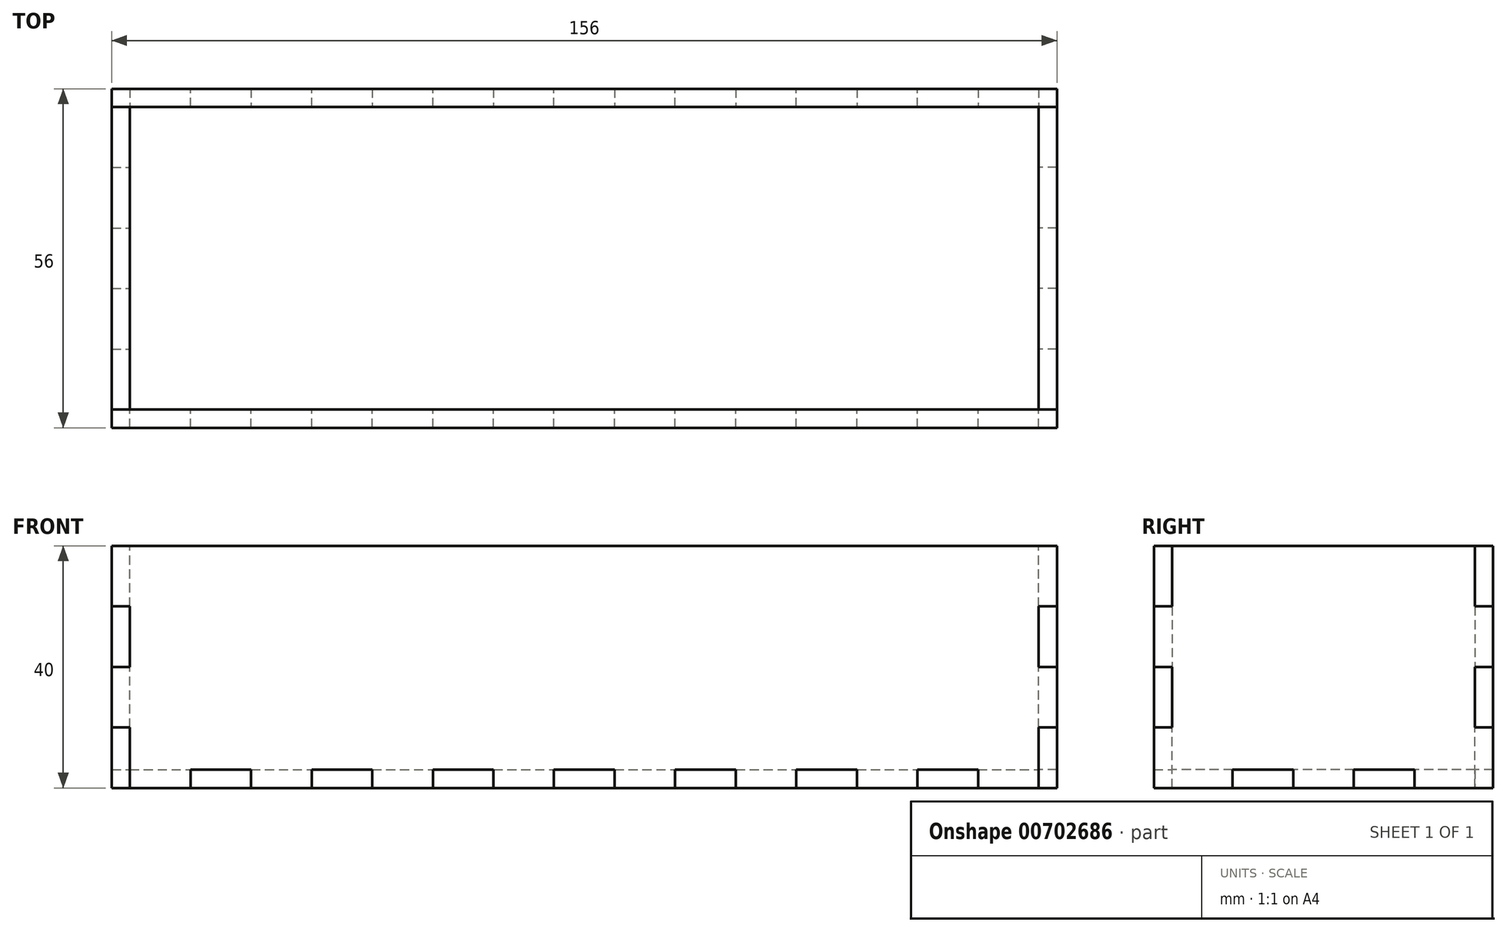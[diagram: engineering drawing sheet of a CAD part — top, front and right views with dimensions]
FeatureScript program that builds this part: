
annotation { "Feature Type Name" : "Feature", "Feature Type Description" : "" }
export const myFeature = defineFeature(function(context is Context, id is Id, definition is map)
    precondition{}
    {
        {
            var Q0;
            Q0=qCreatedBy(makeId("Top.planeOp"),FACE);
            var sketch = newSketch(context, id + "F0", { "sketchPlane" : qUnion([Q0])});
            skPoint(sketch, "E0.middle", {"position": v(0, 0) * mm});
            skLineSegment(sketch, "E1", {"start": v(-75, -25) * mm, "end": v(-65, -25) * mm});
            skLineSegment(sketch, "E2", {"start": v(-65, -25) * mm, "end": v(-65, -28) * mm});
            skLineSegment(sketch, "E3", {"start": v(-65, -28) * mm, "end": v(-55, -28) * mm});
            skLineSegment(sketch, "E4", {"start": v(-55, -28) * mm, "end": v(-55, -25) * mm});
            skLineSegment(sketch, "E5", {"start": v(-55, -25) * mm, "end": v(-45, -25) * mm});
            skLineSegment(sketch, "E6", {"start": v(-45, -25) * mm, "end": v(-45, -28) * mm});
            skLineSegment(sketch, "E7", {"start": v(-45, -28) * mm, "end": v(-35, -28) * mm});
            skLineSegment(sketch, "E8", {"start": v(-35, -28) * mm, "end": v(-35, -25) * mm});
            skLineSegment(sketch, "E9", {"start": v(-35, -25) * mm, "end": v(-25, -25) * mm});
            skLineSegment(sketch, "E10", {"start": v(-25, -25) * mm, "end": v(-25, -28) * mm});
            skLineSegment(sketch, "E11", {"start": v(-25, -28) * mm, "end": v(-15, -28) * mm});
            skLineSegment(sketch, "E12", {"start": v(-15, -28) * mm, "end": v(-15, -25) * mm});
            skLineSegment(sketch, "E13", {"start": v(-15, -25) * mm, "end": v(-5, -25) * mm});
            skLineSegment(sketch, "E14", {"start": v(-5, -25) * mm, "end": v(-5, -28) * mm});
            skLineSegment(sketch, "E15", {"start": v(-5, -28) * mm, "end": v(5, -28) * mm});
            skLineSegment(sketch, "E16", {"start": v(5, -28) * mm, "end": v(5, -25) * mm});
            skLineSegment(sketch, "E17", {"start": v(5, -25) * mm, "end": v(15, -25) * mm});
            skLineSegment(sketch, "E18", {"start": v(15, -25) * mm, "end": v(15, -28) * mm});
            skLineSegment(sketch, "E19", {"start": v(15, -28) * mm, "end": v(25, -28) * mm});
            skLineSegment(sketch, "E20", {"start": v(25, -28) * mm, "end": v(25, -25) * mm});
            skLineSegment(sketch, "E21", {"start": v(25, -25) * mm, "end": v(35, -25) * mm});
            skLineSegment(sketch, "E22", {"start": v(35, -25) * mm, "end": v(35, -28) * mm});
            skLineSegment(sketch, "E23", {"start": v(35, -28) * mm, "end": v(45, -28) * mm});
            skLineSegment(sketch, "E24", {"start": v(45, -28) * mm, "end": v(45, -25) * mm});
            skLineSegment(sketch, "E25", {"start": v(45, -25) * mm, "end": v(55, -25) * mm});
            skLineSegment(sketch, "E26", {"start": v(55, -25) * mm, "end": v(55, -28) * mm});
            skLineSegment(sketch, "E27", {"start": v(55, -28) * mm, "end": v(65, -28) * mm});
            skLineSegment(sketch, "E28", {"start": v(65, -28) * mm, "end": v(65, -25) * mm});
            skLineSegment(sketch, "E29", {"start": v(65, -25) * mm, "end": v(75, -25) * mm});
            skLineSegment(sketch, "E30", {"start": v(-18.9, 0) * mm, "end": v(19.68, 0) * mm, "construction": true});
            skLineSegment(sketch, "E31", {"start": v(0, -7.18) * mm, "end": v(0, 9.4) * mm, "construction": true});
            skLineSegment(sketch, "E32.MirrorCS", {"start": v(35, 25) * mm, "end": v(35, 28) * mm});
            skLineSegment(sketch, "E33.MirrorCS", {"start": v(15, 25) * mm, "end": v(15, 28) * mm});
            skLineSegment(sketch, "E34.MirrorCS", {"start": v(-45, 25) * mm, "end": v(-45, 28) * mm});
            skLineSegment(sketch, "E35.MirrorCS", {"start": v(65, 28) * mm, "end": v(65, 25) * mm});
            skLineSegment(sketch, "E36.MirrorCS", {"start": v(-65, 25) * mm, "end": v(-65, 28) * mm});
            skLineSegment(sketch, "E37.MirrorCS", {"start": v(25, 28) * mm, "end": v(25, 25) * mm});
            skLineSegment(sketch, "E38.MirrorCS", {"start": v(5, 28) * mm, "end": v(5, 25) * mm});
            skLineSegment(sketch, "E39.MirrorCS", {"start": v(-15, 28) * mm, "end": v(-15, 25) * mm});
            skLineSegment(sketch, "E40.MirrorCS", {"start": v(-25, 25) * mm, "end": v(-25, 28) * mm});
            skLineSegment(sketch, "E41.MirrorCS", {"start": v(-75, 25) * mm, "end": v(-65, 25) * mm});
            skLineSegment(sketch, "E42.MirrorCS", {"start": v(-55, 28) * mm, "end": v(-55, 25) * mm});
            skLineSegment(sketch, "E43.MirrorCS", {"start": v(-35, 28) * mm, "end": v(-35, 25) * mm});
            skLineSegment(sketch, "E44.MirrorCS", {"start": v(55, 25) * mm, "end": v(55, 28) * mm});
            skLineSegment(sketch, "E45.MirrorCS", {"start": v(-5, 25) * mm, "end": v(-5, 28) * mm});
            skLineSegment(sketch, "E46.MirrorCS", {"start": v(45, 28) * mm, "end": v(45, 25) * mm});
            skLineSegment(sketch, "E47.MirrorCS", {"start": v(-55, 25) * mm, "end": v(-45, 25) * mm});
            skLineSegment(sketch, "E48.MirrorCS", {"start": v(-15, 25) * mm, "end": v(-5, 25) * mm});
            skLineSegment(sketch, "E49.MirrorCS", {"start": v(5, 25) * mm, "end": v(15, 25) * mm});
            skLineSegment(sketch, "E50.MirrorCS", {"start": v(25, 25) * mm, "end": v(35, 25) * mm});
            skLineSegment(sketch, "E51.MirrorCS", {"start": v(-35, 25) * mm, "end": v(-25, 25) * mm});
            skLineSegment(sketch, "E52.MirrorCS", {"start": v(45, 25) * mm, "end": v(55, 25) * mm});
            skLineSegment(sketch, "E53.MirrorCS", {"start": v(-45, 28) * mm, "end": v(-35, 28) * mm});
            skLineSegment(sketch, "E54.MirrorCS", {"start": v(-25, 28) * mm, "end": v(-15, 28) * mm});
            skLineSegment(sketch, "E55.MirrorCS", {"start": v(-5, 28) * mm, "end": v(5, 28) * mm});
            skLineSegment(sketch, "E56.MirrorCS", {"start": v(55, 28) * mm, "end": v(65, 28) * mm});
            skLineSegment(sketch, "E57.MirrorCS", {"start": v(-65, 28) * mm, "end": v(-55, 28) * mm});
            skLineSegment(sketch, "E58.MirrorCS", {"start": v(65, 25) * mm, "end": v(75, 25) * mm});
            skLineSegment(sketch, "E59.MirrorCS", {"start": v(35, 28) * mm, "end": v(45, 28) * mm});
            skLineSegment(sketch, "E60.MirrorCS", {"start": v(15, 28) * mm, "end": v(25, 28) * mm});
            skPoint(sketch, "E0.right.end.orphan", {"position": v(-75, 25) * mm});
            skLineSegment(sketch, "E61", {"start": v(-75, 25) * mm, "end": v(-75, 15) * mm});
            skLineSegment(sketch, "E62", {"start": v(-75, 15) * mm, "end": v(-78, 15) * mm});
            skLineSegment(sketch, "E63", {"start": v(-78, 15) * mm, "end": v(-78, 5) * mm});
            skLineSegment(sketch, "E64", {"start": v(-78, 5) * mm, "end": v(-75, 5) * mm});
            skLineSegment(sketch, "E65", {"start": v(-75, 5) * mm, "end": v(-75, -5) * mm});
            skLineSegment(sketch, "E66", {"start": v(-75, -5) * mm, "end": v(-78, -5) * mm});
            skLineSegment(sketch, "E67", {"start": v(-78, -5) * mm, "end": v(-78, -15) * mm});
            skLineSegment(sketch, "E68", {"start": v(-78, -15) * mm, "end": v(-75, -15) * mm});
            skLineSegment(sketch, "E69", {"start": v(-75, -15) * mm, "end": v(-75, -25) * mm});
            skPoint(sketch, "E0.left.end.orphan", {"position": v(75, 25) * mm});
            skLineSegment(sketch, "E70.MirrorCS", {"start": v(75, 15) * mm, "end": v(78, 15) * mm});
            skLineSegment(sketch, "E71.MirrorCS", {"start": v(75, 25) * mm, "end": v(75, 15) * mm});
            skLineSegment(sketch, "E72.MirrorCS", {"start": v(78, 5) * mm, "end": v(75, 5) * mm});
            skLineSegment(sketch, "E73.MirrorCS", {"start": v(75, -15) * mm, "end": v(75, -25) * mm});
            skLineSegment(sketch, "E74.MirrorCS", {"start": v(78, -15) * mm, "end": v(75, -15) * mm});
            skLineSegment(sketch, "E75.MirrorCS", {"start": v(75, 5) * mm, "end": v(75, -5) * mm});
            skLineSegment(sketch, "E76.MirrorCS", {"start": v(78, 15) * mm, "end": v(78, 5) * mm});
            skLineSegment(sketch, "E77.MirrorCS", {"start": v(75, -5) * mm, "end": v(78, -5) * mm});
            skLineSegment(sketch, "E78.MirrorCS", {"start": v(78, -5) * mm, "end": v(78, -15) * mm});
            skSolve(sketch);
        }
        {
            var Q0;
            Q0 = qSketchRegion(id + "F0", true);
            extrude(context, id + "F1", {"entities" : qUnion([Q0]), "depth" : 3 * mm, "offsetDistance" : 25 * mm});
        }
        {
            var Q0;
            Q0=makeQuery(id+"F1.opExtrude","SWEPT_FACE",FACE,{"disambiguationData":[OSD([sQuery(id+"F0.wireOp",EDGE,"E65")])]});
            var sketch = newSketch(context, id + "F2", { "sketchPlane" : qUnion([Q0])});
            skLineSegment(sketch, "E79.0.1", {"start": v(-15, 0) * mm, "end": v(-15, 3) * mm});
            skLineSegment(sketch, "E80.0.2", {"start": v(-5, 3) * mm, "end": v(-15, 3) * mm});
            skLineSegment(sketch, "E80.0.3", {"start": v(-15, 3) * mm, "end": v(-15, 0) * mm});
            skLineSegment(sketch, "E81.0.1", {"start": v(15, 0) * mm, "end": v(15, 3) * mm});
            skLineSegment(sketch, "E81.0.2", {"start": v(15, 3) * mm, "end": v(5, 3) * mm});
            skLineSegment(sketch, "E82.0.3", {"start": v(15, 3) * mm, "end": v(15, 0) * mm});
            skPoint(sketch, "E82.0.1.end.orphan", {"position": v(25, 3) * mm});
            skPoint(sketch, "E83.0.1.end.orphan", {"position": v(-25, 3) * mm});
            skPoint(sketch, "E79.0.0.start.orphan", {"position": v(-25, 0) * mm});
            skPoint(sketch, "E82.0.0.end.orphan", {"position": v(25, 0) * mm});
            skLineSegment(sketch, "E84", {"start": v(15, 0) * mm, "end": v(28, 0) * mm});
            skPoint(sketch, "E83.0.3.start.orphan", {"position": v(-28, 3) * mm});
            skPoint(sketch, "E85.0.1.end.orphan", {"position": v(5, 3) * mm});
            skPoint(sketch, "E85.0.3.start.orphan", {"position": v(-5, 3) * mm});
            skLineSegment(sketch, "E86", {"start": v(-5, 3) * mm, "end": v(-5, 0) * mm});
            skLineSegment(sketch, "E87", {"start": v(5, 0) * mm, "end": v(-5, 0) * mm});
            skLineSegment(sketch, "E88", {"start": v(5, 3) * mm, "end": v(5, 0) * mm});
            skLineSegment(sketch, "E89", {"start": v(-28, 10) * mm, "end": v(-25, 10) * mm});
            skLineSegment(sketch, "E90", {"start": v(-25, 10) * mm, "end": v(-25, 20) * mm});
            skLineSegment(sketch, "E91", {"start": v(-25, 20) * mm, "end": v(-28, 20) * mm});
            skPoint(sketch, "E92.0.1.end.orphan", {"position": v(-25, 23) * mm});
            skPoint(sketch, "E92.0.3.start.orphan", {"position": v(-28, 23) * mm});
            skLineSegment(sketch, "E93", {"start": v(-28, 20) * mm, "end": v(-28, 30) * mm});
            skLineSegment(sketch, "E94", {"start": v(-28, 30) * mm, "end": v(-25, 30) * mm});
            skLineSegment(sketch, "E95", {"start": v(-25, 30) * mm, "end": v(-25, 40) * mm});
            skLineSegment(sketch, "E96", {"start": v(0, -5.43) * mm, "end": v(0, 63.92) * mm, "construction": true});
            skPoint(sketch, "E96.endSnap0", {"position": v(0, 3) * mm});
            skPoint(sketch, "E97.orphan", {"position": v(-28, 0) * mm});
            skLineSegment(sketch, "E98", {"start": v(-28, 10) * mm, "end": v(-28, 0) * mm});
            skLineSegment(sketch, "E99", {"start": v(-28, 0) * mm, "end": v(-15, 0) * mm});
            skPoint(sketch, "E100.0.1.end.orphan", {"position": v(28, 3) * mm});
            skLineSegment(sketch, "E101.MirrorCS", {"start": v(28, 10) * mm, "end": v(25, 10) * mm});
            skLineSegment(sketch, "E102.MirrorCS", {"start": v(28, 30) * mm, "end": v(25, 30) * mm});
            skLineSegment(sketch, "E103.MirrorCS", {"start": v(25, 20) * mm, "end": v(28, 20) * mm});
            skLineSegment(sketch, "E104.MirrorCS", {"start": v(25, 30) * mm, "end": v(25, 40) * mm});
            skLineSegment(sketch, "E105.MirrorCS", {"start": v(28, 20) * mm, "end": v(28, 30) * mm});
            skPoint(sketch, "E106.MirrorP", {"position": v(28, 23) * mm});
            skPoint(sketch, "E107.MirrorP", {"position": v(25, 23) * mm});
            skLineSegment(sketch, "E108.MirrorCS", {"start": v(28, 10) * mm, "end": v(28, 0) * mm});
            skLineSegment(sketch, "E109.MirrorCS", {"start": v(25, 10) * mm, "end": v(25, 20) * mm});
            skLineSegment(sketch, "E110", {"start": v(-25, 40) * mm, "end": v(25, 40) * mm});
            skSolve(sketch);
        }
        {
            var Q0;
            Q0 = qSketchRegion(id + "F2", true);
            extrude(context, id + "F3", {"entities" : qUnion([Q0]), "depth" : 3 * mm, "offsetDistance" : 25 * mm});
        }
        {
            var Q0;
            Q0=makeQuery(id+"F1.opExtrude","SWEPT_FACE",FACE,{"disambiguationData":[OSD([sQuery(id+"F0.wireOp",EDGE,"E13")])]});
            var sketch = newSketch(context, id + "F4", { "sketchPlane" : qUnion([Q0])});
            skLineSegment(sketch, "E111.0.0", {"start": v(-75, 0) * mm, "end": v(-65, 0) * mm});
            skLineSegment(sketch, "E111.0.1", {"start": v(-65, 0) * mm, "end": v(-65, 3) * mm});
            skLineSegment(sketch, "E112.0.0", {"start": v(-55, 0) * mm, "end": v(-45, 0) * mm});
            skLineSegment(sketch, "E112.0.1", {"start": v(-45, 0) * mm, "end": v(-45, 3) * mm});
            skLineSegment(sketch, "E112.0.3", {"start": v(-55, 3) * mm, "end": v(-55, 0) * mm});
            skLineSegment(sketch, "E113.0.0", {"start": v(-35, 0) * mm, "end": v(-25, 0) * mm});
            skLineSegment(sketch, "E113.0.1", {"start": v(-25, 0) * mm, "end": v(-25, 3) * mm});
            skLineSegment(sketch, "E113.0.3", {"start": v(-35, 3) * mm, "end": v(-35, 0) * mm});
            skLineSegment(sketch, "E114.0.0", {"start": v(-15, 0) * mm, "end": v(-5, 0) * mm});
            skLineSegment(sketch, "E114.0.1", {"start": v(-5, 0) * mm, "end": v(-5, 3) * mm});
            skLineSegment(sketch, "E114.0.3", {"start": v(-15, 3) * mm, "end": v(-15, 0) * mm});
            skLineSegment(sketch, "E115.0.0", {"start": v(5, 0) * mm, "end": v(15, 0) * mm});
            skLineSegment(sketch, "E115.0.1", {"start": v(15, 0) * mm, "end": v(15, 3) * mm});
            skLineSegment(sketch, "E115.0.3", {"start": v(5, 3) * mm, "end": v(5, 0) * mm});
            skLineSegment(sketch, "E116.0.0", {"start": v(25, 0) * mm, "end": v(35, 0) * mm});
            skLineSegment(sketch, "E116.0.1", {"start": v(35, 0) * mm, "end": v(35, 3) * mm});
            skLineSegment(sketch, "E116.0.3", {"start": v(25, 3) * mm, "end": v(25, 0) * mm});
            skLineSegment(sketch, "E117.0.0", {"start": v(45, 0) * mm, "end": v(55, 0) * mm});
            skLineSegment(sketch, "E117.0.1", {"start": v(55, 0) * mm, "end": v(55, 3) * mm});
            skLineSegment(sketch, "E117.0.3", {"start": v(45, 3) * mm, "end": v(45, 0) * mm});
            skLineSegment(sketch, "E118.0.0", {"start": v(65, 0) * mm, "end": v(75, 0) * mm});
            skLineSegment(sketch, "E118.0.1", {"start": v(75, 0) * mm, "end": v(75, 3) * mm});
            skLineSegment(sketch, "E118.0.3", {"start": v(65, 3) * mm, "end": v(65, 0) * mm});
            skLineSegment(sketch, "E119.0.1", {"start": v(-75, 20) * mm, "end": v(-78, 20) * mm});
            skLineSegment(sketch, "E119.0.2", {"start": v(-78, 20) * mm, "end": v(-78, 10) * mm});
            skLineSegment(sketch, "E119.0.3", {"start": v(-78, 10) * mm, "end": v(-75, 10) * mm});
            skLineSegment(sketch, "E120.0.2", {"start": v(-78, 40) * mm, "end": v(-78, 30) * mm});
            skLineSegment(sketch, "E120.0.3", {"start": v(-78, 30) * mm, "end": v(-75, 30) * mm});
            skPoint(sketch, "E111.0.3.start.orphan", {"position": v(-75, 3) * mm});
            skLineSegment(sketch, "E121", {"start": v(-75, 10) * mm, "end": v(-75, 0) * mm});
            skLineSegment(sketch, "E122", {"start": v(-75, 30) * mm, "end": v(-75, 20) * mm});
            skLineSegment(sketch, "E123", {"start": v(-65, 3) * mm, "end": v(-55, 3) * mm});
            skLineSegment(sketch, "E124", {"start": v(-45, 3) * mm, "end": v(-35, 3) * mm});
            skLineSegment(sketch, "E125", {"start": v(-25, 3) * mm, "end": v(-15, 3) * mm});
            skLineSegment(sketch, "E126", {"start": v(-5, 3) * mm, "end": v(5, 3) * mm});
            skLineSegment(sketch, "E127", {"start": v(15, 3) * mm, "end": v(25, 3) * mm});
            skLineSegment(sketch, "E128", {"start": v(35, 3) * mm, "end": v(45, 3) * mm});
            skLineSegment(sketch, "E129", {"start": v(55, 3) * mm, "end": v(65, 3) * mm});
            skLineSegment(sketch, "E130", {"start": v(0, -10.28) * mm, "end": v(0, 33.96) * mm, "construction": true});
            skPoint(sketch, "E120.0.1.start.orphan", {"position": v(-75, 40) * mm});
            skLineSegment(sketch, "E131.MirrorCS", {"start": v(75, 20) * mm, "end": v(78, 20) * mm});
            skLineSegment(sketch, "E132.MirrorCS", {"start": v(75, 30) * mm, "end": v(75, 20) * mm});
            skLineSegment(sketch, "E133.MirrorCS", {"start": v(78, 40) * mm, "end": v(78, 30) * mm});
            skLineSegment(sketch, "E134.MirrorCS", {"start": v(78, 10) * mm, "end": v(75, 10) * mm});
            skLineSegment(sketch, "E135.MirrorCS", {"start": v(78, 30) * mm, "end": v(75, 30) * mm});
            skPoint(sketch, "E136.MirrorP", {"position": v(75, 40) * mm});
            skLineSegment(sketch, "E137.MirrorCS", {"start": v(75, 10) * mm, "end": v(75, 0) * mm});
            skLineSegment(sketch, "E138.MirrorCS", {"start": v(78, 20) * mm, "end": v(78, 10) * mm});
            skPoint(sketch, "E139.MirrorP", {"position": v(75, 3) * mm});
            skPoint(sketch, "E140.MirrorCS.end.orphan", {"position": v(65, 0) * mm});
            skLineSegment(sketch, "E141", {"start": v(-78, 40) * mm, "end": v(78, 40) * mm});
            skSolve(sketch);
        }
        {
            var Q0;
            Q0 = qSketchRegion(id + "F4", true);
            extrude(context, id + "F5", {"entities" : qUnion([Q0]), "depth" : 3 * mm, "offsetDistance" : 25 * mm});
        }
        {
            var Q0;
            Q0=makeQuery(id+"F3.opExtrude","SWEPT_BODY",BODY,{"disambiguationData":[OSD([sQuery(id+"F2.wireOp",EDGE,"E80.0.2"),sQuery(id+"F2.wireOp",EDGE,"E80.0.3"),sQuery(id+"F2.wireOp",EDGE,"E81.0.2"),sQuery(id+"F2.wireOp",EDGE,"E82.0.3"),sQuery(id+"F2.wireOp",EDGE,"E84"),sQuery(id+"F2.wireOp",EDGE,"E86"),sQuery(id+"F2.wireOp",EDGE,"E87"),sQuery(id+"F2.wireOp",EDGE,"E88"),sQuery(id+"F2.wireOp",EDGE,"E89"),sQuery(id+"F2.wireOp",EDGE,"E90"),sQuery(id+"F2.wireOp",EDGE,"E91"),sQuery(id+"F2.wireOp",EDGE,"E93"),sQuery(id+"F2.wireOp",EDGE,"E94"),sQuery(id+"F2.wireOp",EDGE,"E95"),sQuery(id+"F2.wireOp",EDGE,"E98"),sQuery(id+"F2.wireOp",EDGE,"E99"),sQuery(id+"F2.wireOp",EDGE,"E101.MirrorCS"),sQuery(id+"F2.wireOp",EDGE,"E102.MirrorCS"),sQuery(id+"F2.wireOp",EDGE,"E103.MirrorCS"),sQuery(id+"F2.wireOp",EDGE,"E104.MirrorCS"),sQuery(id+"F2.wireOp",EDGE,"E105.MirrorCS"),sQuery(id+"F2.wireOp",EDGE,"E108.MirrorCS"),sQuery(id+"F2.wireOp",EDGE,"E109.MirrorCS"),sQuery(id+"F2.wireOp",EDGE,"E110")])]});
            var Q1;
            Q1=qCreatedBy(makeId("Right.planeOp"),FACE);
            mirror(context, id + "F6", {"entities" : qUnion([Q0]), "mirrorPlane" : qUnion([Q1])});
        }
        {
            var Q0;
            Q0=makeQuery(id+"F5.opExtrude","SWEPT_BODY",BODY,{"disambiguationData":[OSD([sQuery(id+"F4.wireOp",EDGE,"E111.0.0"),sQuery(id+"F4.wireOp",EDGE,"E111.0.1"),sQuery(id+"F4.wireOp",EDGE,"E112.0.0"),sQuery(id+"F4.wireOp",EDGE,"E112.0.1"),sQuery(id+"F4.wireOp",EDGE,"E112.0.3"),sQuery(id+"F4.wireOp",EDGE,"E113.0.0"),sQuery(id+"F4.wireOp",EDGE,"E113.0.1"),sQuery(id+"F4.wireOp",EDGE,"E113.0.3"),sQuery(id+"F4.wireOp",EDGE,"E114.0.0"),sQuery(id+"F4.wireOp",EDGE,"E114.0.1"),sQuery(id+"F4.wireOp",EDGE,"E114.0.3"),sQuery(id+"F4.wireOp",EDGE,"E115.0.0"),sQuery(id+"F4.wireOp",EDGE,"E115.0.1"),sQuery(id+"F4.wireOp",EDGE,"E115.0.3"),sQuery(id+"F4.wireOp",EDGE,"E116.0.0"),sQuery(id+"F4.wireOp",EDGE,"E116.0.1"),sQuery(id+"F4.wireOp",EDGE,"E116.0.3"),sQuery(id+"F4.wireOp",EDGE,"E117.0.0"),sQuery(id+"F4.wireOp",EDGE,"E117.0.1"),sQuery(id+"F4.wireOp",EDGE,"E117.0.3"),sQuery(id+"F4.wireOp",EDGE,"E118.0.0"),sQuery(id+"F4.wireOp",EDGE,"E118.0.3"),sQuery(id+"F4.wireOp",EDGE,"E119.0.1"),sQuery(id+"F4.wireOp",EDGE,"E119.0.2"),sQuery(id+"F4.wireOp",EDGE,"E119.0.3"),sQuery(id+"F4.wireOp",EDGE,"E120.0.2"),sQuery(id+"F4.wireOp",EDGE,"E120.0.3"),sQuery(id+"F4.wireOp",EDGE,"E121"),sQuery(id+"F4.wireOp",EDGE,"E122"),sQuery(id+"F4.wireOp",EDGE,"E123"),sQuery(id+"F4.wireOp",EDGE,"E124"),sQuery(id+"F4.wireOp",EDGE,"E125"),sQuery(id+"F4.wireOp",EDGE,"E126"),sQuery(id+"F4.wireOp",EDGE,"E127"),sQuery(id+"F4.wireOp",EDGE,"E128"),sQuery(id+"F4.wireOp",EDGE,"E129"),sQuery(id+"F4.wireOp",EDGE,"E131.MirrorCS"),sQuery(id+"F4.wireOp",EDGE,"E132.MirrorCS"),sQuery(id+"F4.wireOp",EDGE,"E133.MirrorCS"),sQuery(id+"F4.wireOp",EDGE,"E134.MirrorCS"),sQuery(id+"F4.wireOp",EDGE,"E135.MirrorCS"),sQuery(id+"F4.wireOp",EDGE,"E137.MirrorCS"),sQuery(id+"F4.wireOp",EDGE,"E138.MirrorCS"),sQuery(id+"F4.wireOp",EDGE,"E141")])]});
            var Q1;
            Q1=qCreatedBy(makeId("Front.planeOp"),FACE);
            mirror(context, id + "F7", {"entities" : qUnion([Q0]), "mirrorPlane" : qUnion([Q1])});
        }
    });
